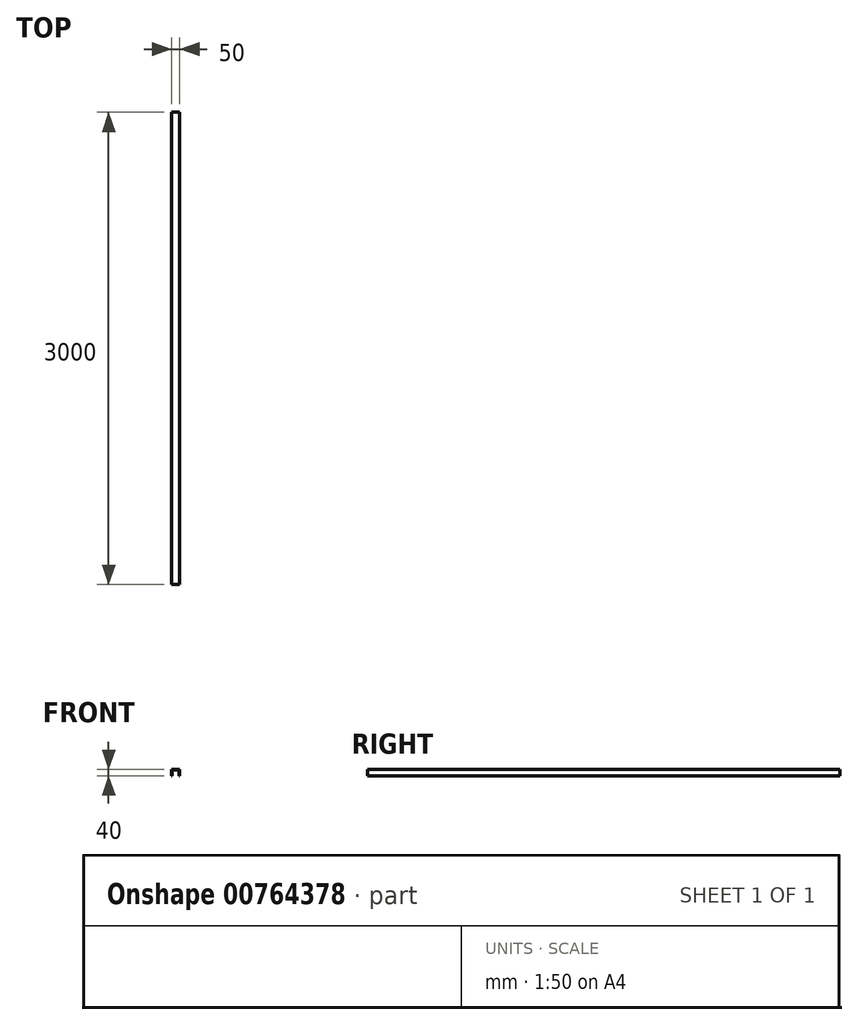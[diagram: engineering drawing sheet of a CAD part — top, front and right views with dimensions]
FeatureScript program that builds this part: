
annotation { "Feature Type Name" : "Feature", "Feature Type Description" : "" }
export const myFeature = defineFeature(function(context is Context, id is Id, definition is map)
    precondition{}
    {
        {
            var Q0;
            Q0=qCreatedBy(makeId("Front.planeOp"),FACE);
            var sketch = newSketch(context, id + "F0", { "sketchPlane" : qUnion([Q0])});
            skLineSegment(sketch, "E0", {"start": v(-30, 0) * mm, "end": v(-30, 40) * mm});
            skLineSegment(sketch, "E1", {"start": v(-30, 40) * mm, "end": v(20, 40) * mm});
            skLineSegment(sketch, "E2.1", {"start": v(-27, 37) * mm, "end": v(17, 37) * mm});
            skLineSegment(sketch, "E2.2", {"start": v(-27, 0) * mm, "end": v(-27, 37) * mm});
            skLineSegment(sketch, "E3", {"start": v(-30, 0) * mm, "end": v(-27, 0) * mm});
            skLineSegment(sketch, "E4", {"start": v(20, 40) * mm, "end": v(20, 0) * mm});
            skLineSegment(sketch, "E5", {"start": v(20, 0) * mm, "end": v(17, 0) * mm});
            skLineSegment(sketch, "E6", {"start": v(17, 0) * mm, "end": v(17, 37) * mm});
            skSolve(sketch);
        }
        {
            var Q0;
            Q0=makeQuery(id+"F0.imprint","IMPRINT",FACE,{"disambiguationData":[TD([[makeQuery(id+"F0.imprint","IMPRINT",EDGE,{"derivedFrom":sQuery(id+"F0.wireOp",EDGE,"E0")}),-1.0]])]});
            extrude(context, id + "F1", {"entities" : qUnion([Q0]), "depth" : 3000 * mm, "offsetDistance" : 25 * mm, "symmetric" : true});
        }
    });
